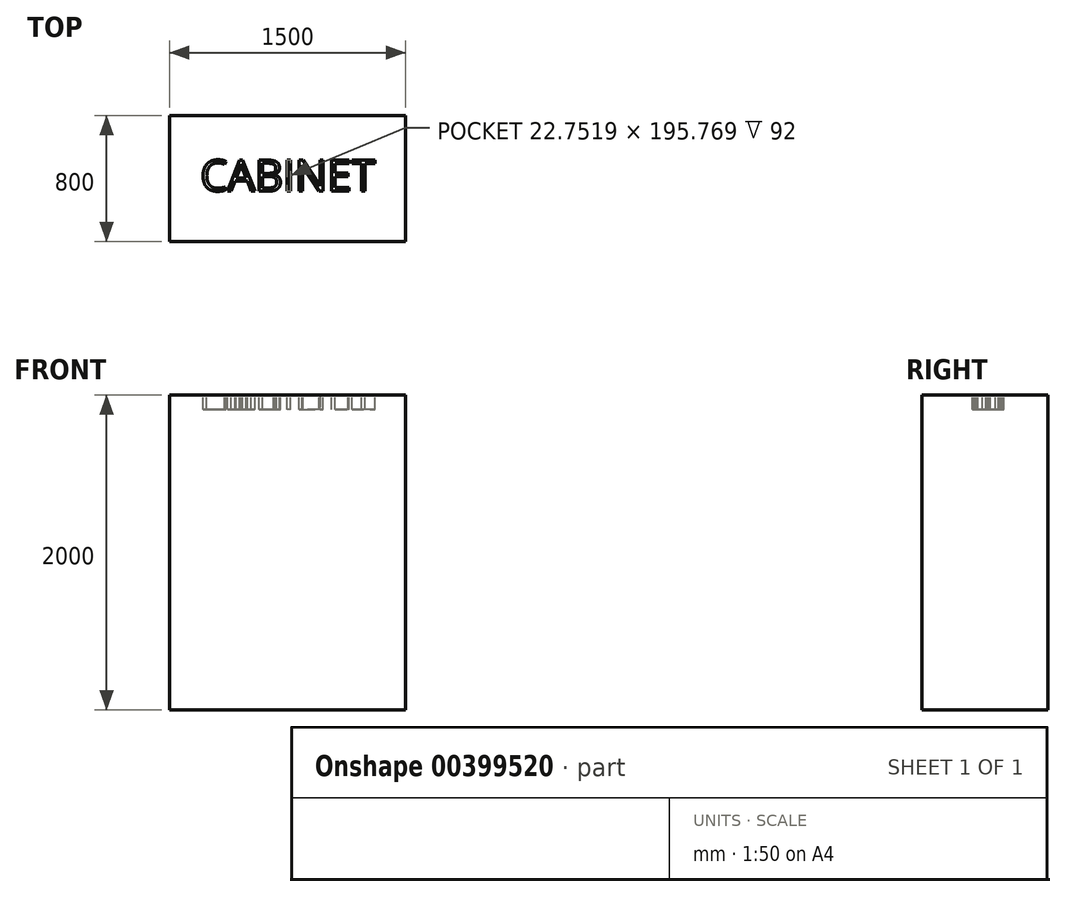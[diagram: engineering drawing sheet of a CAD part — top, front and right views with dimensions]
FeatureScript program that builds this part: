
annotation { "Feature Type Name" : "Feature", "Feature Type Description" : "" }
export const myFeature = defineFeature(function(context is Context, id is Id, definition is map)
    precondition{}
    {
        {
            var Q0;
            Q0=qCreatedBy(makeId("Top.planeOp"),FACE);
            var sketch = newSketch(context, id + "F0", { "sketchPlane" : qUnion([Q0])});
            skLineSegment(sketch, "E0.bottom", {"start": v(750, -400) * mm, "end": v(-750, -400) * mm});
            skLineSegment(sketch, "E0.top", {"start": v(750, 400) * mm, "end": v(-750, 400) * mm});
            skLineSegment(sketch, "E0.left", {"start": v(750, -400) * mm, "end": v(750, 400) * mm});
            skLineSegment(sketch, "E0.right", {"start": v(-750, -400) * mm, "end": v(-750, 400) * mm});
            skPoint(sketch, "E0.middle", {"position": v(0, 0) * mm});
            skSolve(sketch);
        }
        {
            var Q0;
            Q0 = qSketchRegion(id + "F0", true);
            extrude(context, id + "F1", {"entities" : qUnion([Q0]), "depth" : 2000 * mm});
        }
        {
            var Q0;
            Q0=makeQuery(id+"F1.opExtrude","CAP_FACE",FACE,{"disambiguationData":[OSD([sQuery(id+"F0.wireOp",EDGE,"E0.bottom"),sQuery(id+"F0.wireOp",EDGE,"E0.top"),sQuery(id+"F0.wireOp",EDGE,"E0.left"),sQuery(id+"F0.wireOp",EDGE,"E0.right")])],"isStart":false});
            var sketch = newSketch(context, id + "F2", { "sketchPlane" : qUnion([Q0])});
            skText(sketch, "E1", { "text": "CABINET", "fontName": "OpenSans-Regular.ttf"});
            const initialGuessF2  = {"E1": [-0.55423, -0.0788, 1, 0, 0.19744]};
            skSetInitialGuess(sketch, initialGuessF2);
            skSolve(sketch);
        }
        {
            var Q0;
            Q0 = qSketchRegion(id + "F2", true);
            extrude(context, id + "F3", {"entities" : qUnion([Q0]), "operationType" : NewBodyOperationType.REMOVE, "oppositeDirection" : true, "depth" : 92 * mm});
        }
    });
